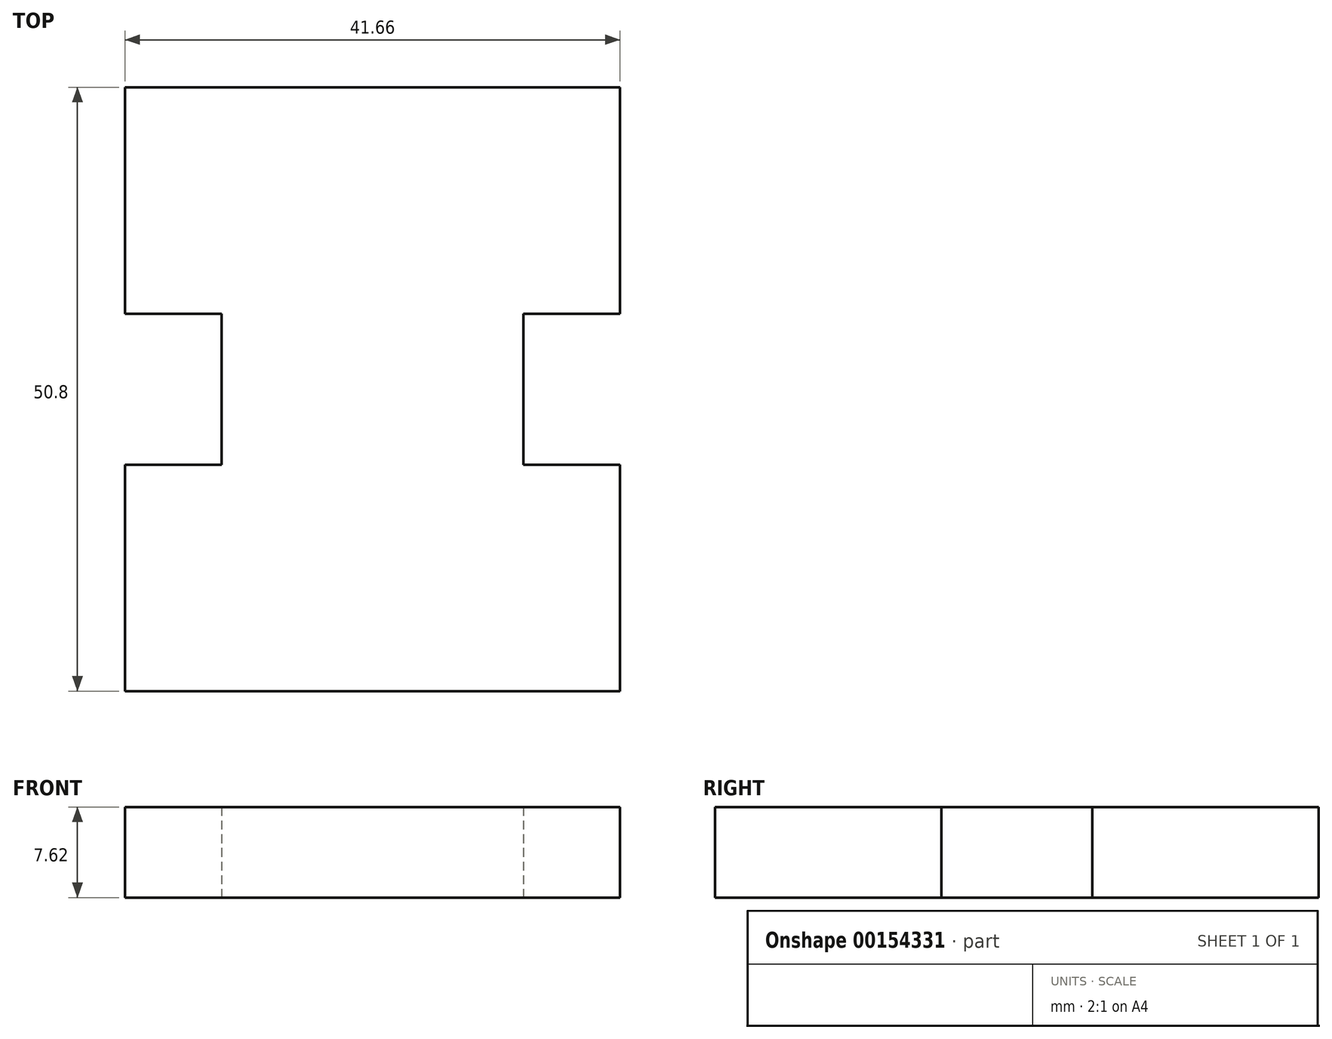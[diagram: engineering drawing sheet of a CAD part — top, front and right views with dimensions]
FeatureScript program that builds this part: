
annotation { "Feature Type Name" : "Feature", "Feature Type Description" : "" }
export const myFeature = defineFeature(function(context is Context, id is Id, definition is map)
    precondition{}
    {
        {
            var Q0;
            Q0=qCreatedBy(makeId("Top.planeOp"),FACE);
            var sketch = newSketch(context, id + "F0", { "sketchPlane" : qUnion([Q0])});
            skLineSegment(sketch, "E0", {"start": v(0, 0) * mm, "end": v(-8.13, 0) * mm});
            skLineSegment(sketch, "E1", {"start": v(-8.13, 0) * mm, "end": v(-8.13, 19.05) * mm});
            skLineSegment(sketch, "E2", {"start": v(-8.13, 19.05) * mm, "end": v(0, 19.05) * mm});
            skLineSegment(sketch, "E3", {"start": v(0, 19.05) * mm, "end": v(0, 31.75) * mm});
            skLineSegment(sketch, "E4", {"start": v(0, 31.75) * mm, "end": v(-8.13, 31.75) * mm});
            skLineSegment(sketch, "E5", {"start": v(-8.13, 31.75) * mm, "end": v(-8.13, 50.8) * mm});
            skLineSegment(sketch, "E6", {"start": v(-8.13, 50.8) * mm, "end": v(0, 50.8) * mm});
            skLineSegment(sketch, "E7", {"start": v(0, 50.8) * mm, "end": v(25.4, 50.8) * mm});
            skLineSegment(sketch, "E8", {"start": v(25.4, 50.8) * mm, "end": v(33.53, 50.8) * mm});
            skLineSegment(sketch, "E9", {"start": v(33.53, 50.8) * mm, "end": v(33.53, 31.75) * mm});
            skLineSegment(sketch, "E10", {"start": v(33.53, 31.75) * mm, "end": v(25.4, 31.75) * mm});
            skLineSegment(sketch, "E11", {"start": v(25.4, 31.75) * mm, "end": v(25.4, 19.05) * mm});
            skLineSegment(sketch, "E12", {"start": v(25.4, 19.05) * mm, "end": v(33.53, 19.05) * mm});
            skLineSegment(sketch, "E13", {"start": v(33.53, 19.05) * mm, "end": v(33.53, 0) * mm});
            skLineSegment(sketch, "E14", {"start": v(33.53, 0) * mm, "end": v(0, 0) * mm});
            skSolve(sketch);
        }
        {
            var Q0;
            Q0=makeQuery(id+"F0.imprint","IMPRINT",FACE,{"disambiguationData":[TD([[makeQuery(id+"F0.imprint","IMPRINT",EDGE,{"derivedFrom":sQuery(id+"F0.wireOp",EDGE,"E0")}),-1.0]])]});
            extrude(context, id + "F1", {"entities" : qUnion([Q0]), "endBound" : BoundingType.SYMMETRIC, "depth" : 7.62 * mm});
        }
    });
